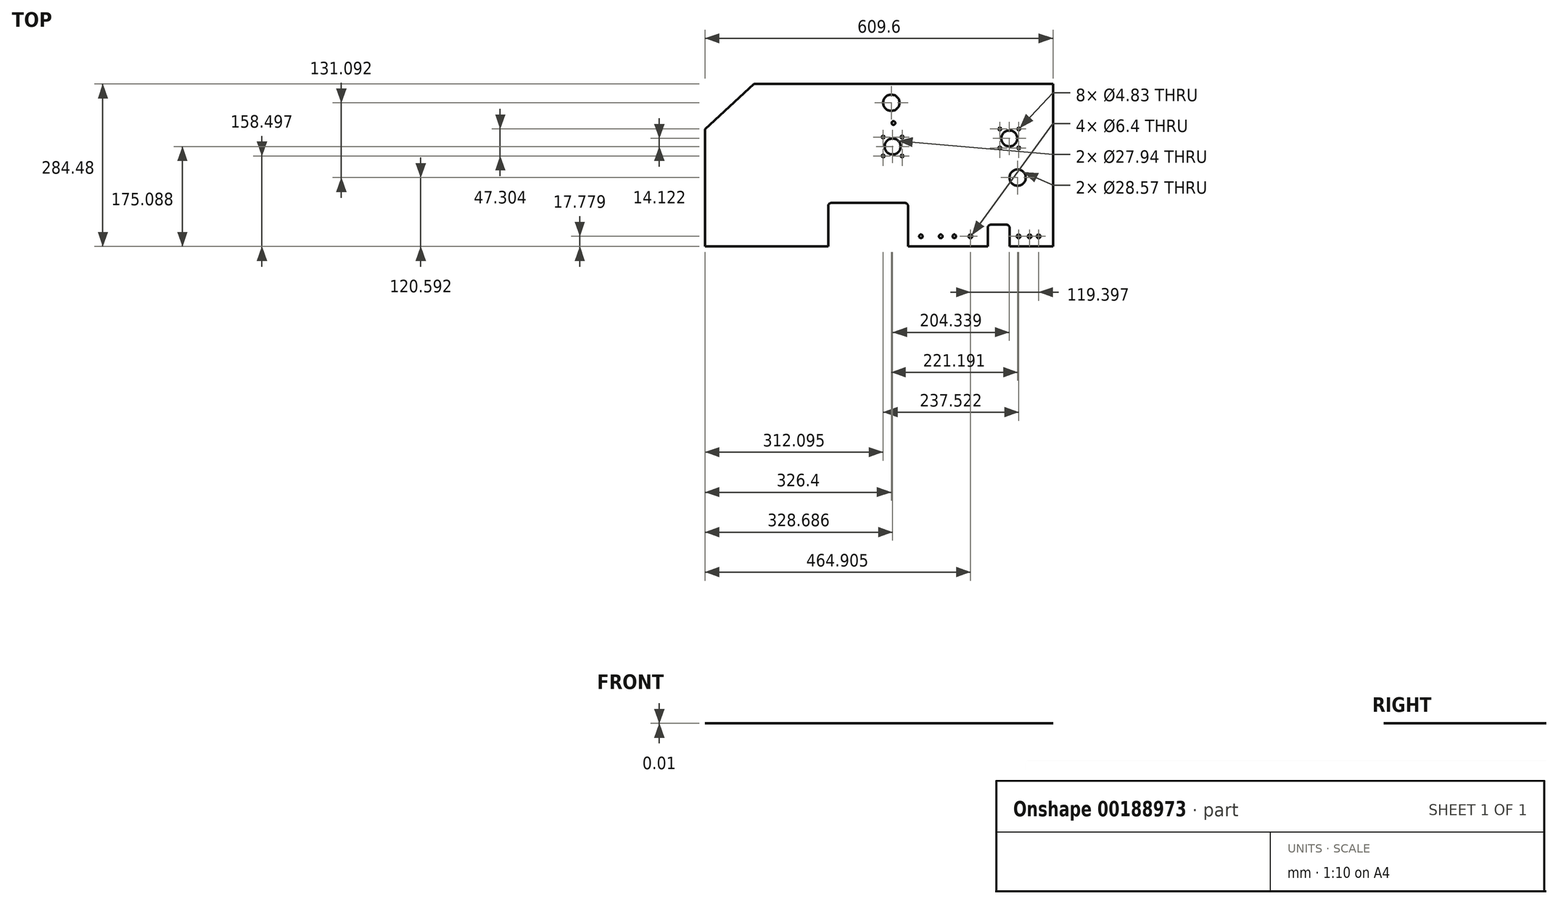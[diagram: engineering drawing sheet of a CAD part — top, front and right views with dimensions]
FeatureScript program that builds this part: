
annotation { "Feature Type Name" : "Feature", "Feature Type Description" : "" }
export const myFeature = defineFeature(function(context is Context, id is Id, definition is map)
    precondition{}
    {
        {
            var Q0;
            Q0=qCreatedBy(makeId("Top.planeOp"),FACE);
            var sketch = newSketch(context, id + "F0", { "sketchPlane" : qUnion([Q0])});
            skLineSegment(sketch, "E0.bottom", {"start": v(46.08, 36.72) * mm, "end": v(570.04, 36.72) * mm});
            skLineSegment(sketch, "E0.top", {"start": v(-39.56, -247.76) * mm, "end": v(176.34, -247.76) * mm});
            skLineSegment(sketch, "E0.left", {"start": v(-39.56, -42.66) * mm, "end": v(-39.56, -247.76) * mm});
            skLineSegment(sketch, "E0.right", {"start": v(570.04, 36.72) * mm, "end": v(570.04, -247.76) * mm});
            skLineSegment(sketch, "E1", {"start": v(-39.56, -42.66) * mm, "end": v(46.08, 36.72) * mm});
            skLineSegment(sketch, "E2.bottom", {"start": v(570.04, -247.76) * mm, "end": v(493.84, -247.76) * mm, "construction": true});
            skLineSegment(sketch, "E2.top", {"start": v(570.04, 36.72) * mm, "end": v(-39.56, 36.72) * mm, "construction": true});
            skLineSegment(sketch, "E2.left", {"start": v(570.04, -247.76) * mm, "end": v(570.04, 36.72) * mm, "construction": true});
            skLineSegment(sketch, "E2.right", {"start": v(-39.56, -247.76) * mm, "end": v(-39.56, 36.72) * mm, "construction": true});
            skCircle(sketch, "E3", {"center": v(508.03, -127.17) * mm, "radius": 14.29 * mm});
            skCircle(sketch, "E4", {"center": v(493.47, -58.55) * mm, "radius": 23.46 * mm, "construction": true});
            skLineSegment(sketch, "E5.bottom", {"start": v(476.87, -41.96) * mm, "end": v(510.06, -41.96) * mm, "construction": true});
            skLineSegment(sketch, "E5.top", {"start": v(476.87, -75.14) * mm, "end": v(510.06, -75.14) * mm, "construction": true});
            skLineSegment(sketch, "E5.left", {"start": v(476.87, -41.96) * mm, "end": v(476.87, -75.14) * mm, "construction": true});
            skLineSegment(sketch, "E5.right", {"start": v(510.06, -41.96) * mm, "end": v(510.06, -75.14) * mm, "construction": true});
            skCircle(sketch, "E6", {"center": v(476.87, -41.96) * mm, "radius": 2.41 * mm});
            skCircle(sketch, "E7", {"center": v(510.06, -41.96) * mm, "radius": 2.41 * mm});
            skCircle(sketch, "E8", {"center": v(510.06, -75.14) * mm, "radius": 2.41 * mm});
            skCircle(sketch, "E9", {"center": v(476.87, -75.14) * mm, "radius": 2.41 * mm});
            skCircle(sketch, "E10", {"center": v(493.47, -58.55) * mm, "radius": 13.97 * mm});
            skCircle(sketch, "E11", {"center": v(286.84, 3.92) * mm, "radius": 14.29 * mm});
            skLineSegment(sketch, "E12", {"start": v(455.74, -247.76) * mm, "end": v(455.74, -209.66) * mm});
            skLineSegment(sketch, "E13", {"start": v(455.74, -209.66) * mm, "end": v(493.84, -209.66) * mm});
            skLineSegment(sketch, "E14", {"start": v(493.84, -209.66) * mm, "end": v(493.84, -247.76) * mm});
            skLineSegment(sketch, "E15.trimOffspring", {"start": v(455.74, -247.76) * mm, "end": v(316.04, -247.76) * mm, "construction": true});
            skCircle(sketch, "E16", {"center": v(289.13, -72.67) * mm, "radius": 23.46 * mm, "construction": true});
            skLineSegment(sketch, "E17.bottom", {"start": v(272.53, -56.08) * mm, "end": v(305.72, -56.08) * mm, "construction": true});
            skLineSegment(sketch, "E17.top", {"start": v(272.53, -89.26) * mm, "end": v(305.72, -89.26) * mm, "construction": true});
            skLineSegment(sketch, "E17.left", {"start": v(272.53, -56.08) * mm, "end": v(272.53, -89.26) * mm, "construction": true});
            skLineSegment(sketch, "E17.right", {"start": v(305.72, -56.08) * mm, "end": v(305.72, -89.26) * mm, "construction": true});
            skCircle(sketch, "E18", {"center": v(272.53, -56.08) * mm, "radius": 2.41 * mm});
            skCircle(sketch, "E19", {"center": v(305.72, -56.08) * mm, "radius": 2.41 * mm});
            skCircle(sketch, "E20", {"center": v(305.72, -89.26) * mm, "radius": 2.41 * mm});
            skCircle(sketch, "E21", {"center": v(272.53, -89.26) * mm, "radius": 2.41 * mm});
            skCircle(sketch, "E22", {"center": v(289.13, -72.67) * mm, "radius": 13.97 * mm});
            skLineSegment(sketch, "E23.top", {"start": v(176.34, -171.56) * mm, "end": v(316.04, -171.56) * mm});
            skLineSegment(sketch, "E23.left", {"start": v(176.34, -247.76) * mm, "end": v(176.34, -171.56) * mm});
            skLineSegment(sketch, "E23.right", {"start": v(316.04, -247.76) * mm, "end": v(316.04, -171.56) * mm});
            skLineSegment(sketch, "E24.trimOffspring", {"start": v(176.34, -247.76) * mm, "end": v(-39.56, -247.76) * mm, "construction": true});
            skLineSegment(sketch, "E25.trimOffspring", {"start": v(316.04, -247.76) * mm, "end": v(570.04, -247.76) * mm});
            skCircle(sketch, "E26", {"center": v(290.56, -31.56) * mm, "radius": 3.18 * mm});
            skCircle(sketch, "E27", {"center": v(338.7, -229.98) * mm, "radius": 3.18 * mm});
            skCircle(sketch, "E28", {"center": v(373.4, -229.98) * mm, "radius": 3.18 * mm});
            skCircle(sketch, "E29", {"center": v(397.14, -229.98) * mm, "radius": 3.18 * mm});
            skCircle(sketch, "E30", {"center": v(425.34, -229.98) * mm, "radius": 3.2 * mm});
            skCircle(sketch, "E31", {"center": v(509.72, -229.98) * mm, "radius": 3.2 * mm});
            skCircle(sketch, "E32", {"center": v(544.74, -229.98) * mm, "radius": 3.2 * mm});
            skCircle(sketch, "E33", {"center": v(529, -229.98) * mm, "radius": 3.2 * mm});
            skCircle(sketch, "E34", {"center": v(475.54, -228.45) * mm, "radius": 6.35 * mm});
            skSolve(sketch);
        }
        {
            var Q0;
            Q0=makeQuery(id+"F0.imprint","IMPRINT",FACE,{"disambiguationData":[TD([[makeQuery(id+"F0.imprint","IMPRINT",EDGE,{"derivedFrom":sQuery(id+"F0.wireOp",EDGE,"E0.bottom")}),-1.0]])]});
            extrude(context, id + "F1", {"entities" : qUnion([Q0]), "depth" : 1 / 101.6 * mm});
        }
        {
            var Q0;
            Q0=makeQuery(id+"F1.opExtrude","SWEPT_EDGE",EDGE,{"disambiguationData":[OSD([sQuery(id+"F0.wireOp",EDGE,"E23.top"),sQuery(id+"F0.wireOp",EDGE,"E23.left")])]});
            var Q1;
            Q1=makeQuery(id+"F1.opExtrude","SWEPT_EDGE",EDGE,{"disambiguationData":[OSD([sQuery(id+"F0.wireOp",EDGE,"E23.top"),sQuery(id+"F0.wireOp",EDGE,"E23.right")])]});
            var Q2;
            Q2=makeQuery(id+"F1.opExtrude","SWEPT_EDGE",EDGE,{"disambiguationData":[OSD([sQuery(id+"F0.wireOp",EDGE,"E12"),sQuery(id+"F0.wireOp",EDGE,"E13")])]});
            var Q3;
            Q3=makeQuery(id+"F1.opExtrude","SWEPT_EDGE",EDGE,{"disambiguationData":[OSD([sQuery(id+"F0.wireOp",EDGE,"E13"),sQuery(id+"F0.wireOp",EDGE,"E14")])]});
            fillet(context, id + "F2", {"entities" : qUnion([Q0, Q1, Q2, Q3]), "radius" : 5.08 * mm, "tangentPropagation" : true, "allowEdgeOverflow" : false});
        }
    });
